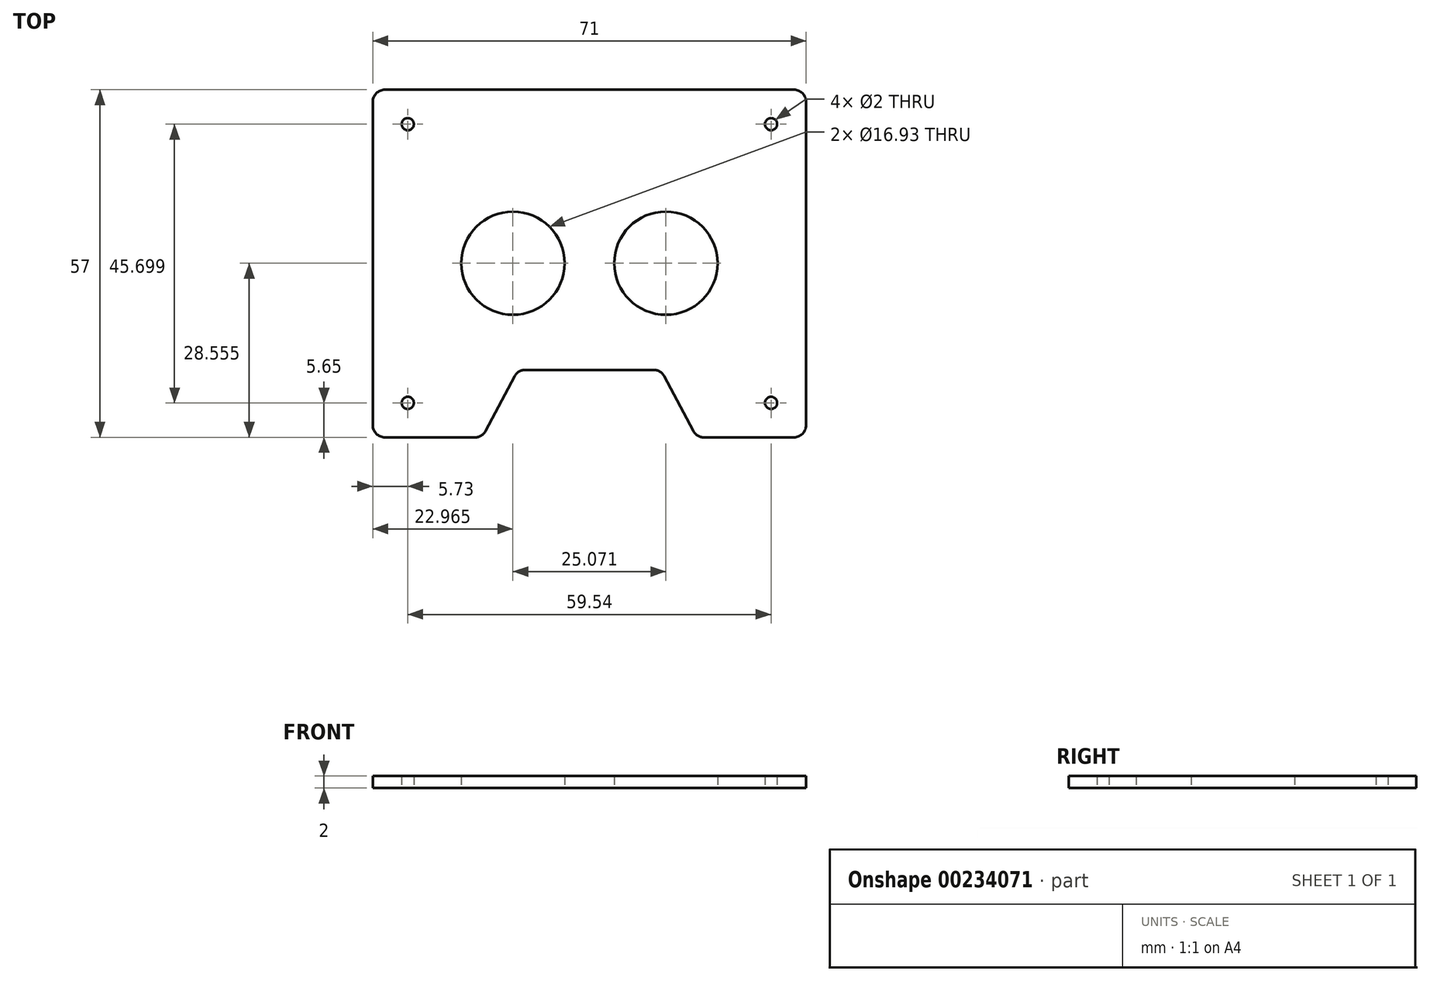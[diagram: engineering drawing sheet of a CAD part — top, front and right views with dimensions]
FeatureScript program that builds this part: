
annotation { "Feature Type Name" : "Feature", "Feature Type Description" : "" }
export const myFeature = defineFeature(function(context is Context, id is Id, definition is map)
    precondition{}
    {
        {
            var Q0;
            Q0=qCreatedBy(makeId("Top.planeOp"),FACE);
            var sketch = newSketch(context, id + "F0", { "sketchPlane" : qUnion([Q0])});
            skLineSegment(sketch, "E0.bottom", {"start": v(21, -8.5) * mm, "end": v(-21, -8.5) * mm, "construction": true});
            skLineSegment(sketch, "E0.top", {"start": v(21, 8.5) * mm, "end": v(-21, 8.5) * mm, "construction": true});
            skLineSegment(sketch, "E0.left", {"start": v(21, -8.5) * mm, "end": v(21, 8.5) * mm, "construction": true});
            skLineSegment(sketch, "E0.right", {"start": v(-21, -8.5) * mm, "end": v(-21, 8.5) * mm, "construction": true});
            skPoint(sketch, "E0.middle", {"position": v(0, 0) * mm});
            skLineSegment(sketch, "E1.bottom", {"start": v(35.5, -28.5) * mm, "end": v(17.56, -28.5) * mm});
            skLineSegment(sketch, "E1.top", {"start": v(35.5, 28.5) * mm, "end": v(-35.5, 28.5) * mm});
            skLineSegment(sketch, "E1.left", {"start": v(35.5, -28.5) * mm, "end": v(35.5, 28.5) * mm});
            skLineSegment(sketch, "E1.right", {"start": v(-35.5, -28.5) * mm, "end": v(-35.5, 28.5) * mm});
            skPoint(sketch, "E2", {"position": v(-29.77, 22.85) * mm});
            skPoint(sketch, "E3.MirrorP", {"position": v(29.77, 22.85) * mm});
            skPoint(sketch, "E4.MirrorP", {"position": v(-29.77, -22.85) * mm});
            skPoint(sketch, "E5.MirrorP", {"position": v(29.77, -22.85) * mm});
            skCircle(sketch, "E6", {"center": v(-12.54, 0.06) * mm, "radius": 8.46 * mm});
            skPoint(sketch, "E6.first.point", {"position": v(-21, 0) * mm});
            skPoint(sketch, "E6.second.point", {"position": v(-4.07, 0) * mm});
            skPoint(sketch, "E6.second.point.positionSnap0", {"position": v(-21, 0) * mm});
            skPoint(sketch, "E6.third.point", {"position": v(-11.96, 8.5) * mm});
            skPoint(sketch, "E7.MirrorP", {"position": v(4.07, 0) * mm});
            skCircle(sketch, "E8.MirrorC", {"center": v(12.54, 0.06) * mm, "radius": 8.46 * mm});
            skLineSegment(sketch, "E9", {"start": v(-17.56, -28.5) * mm, "end": v(-11.7, -17.43) * mm});
            skLineSegment(sketch, "E10", {"start": v(-11.7, -17.43) * mm, "end": v(0, -17.43) * mm});
            skLineSegment(sketch, "E11.MirrorCS", {"start": v(11.7, -17.43) * mm, "end": v(0, -17.43) * mm});
            skLineSegment(sketch, "E12.MirrorCS", {"start": v(17.56, -28.5) * mm, "end": v(11.7, -17.43) * mm});
            skLineSegment(sketch, "E13.trimOffspring", {"start": v(-17.56, -28.5) * mm, "end": v(-35.5, -28.5) * mm});
            skSolve(sketch);
        }
        {
            var Q0;
            Q0 = qSketchRegion(id + "F0", true);
            extrude(context, id + "F1", {"entities" : qUnion([Q0]), "depth" : 2 * mm});
        }
        {
            var Q0;
            Q0=makeQuery(id+"F1.opExtrude","SWEPT_EDGE",EDGE,{"disambiguationData":[OSD([sQuery(id+"F0.wireOp",EDGE,"E1.top"),sQuery(id+"F0.wireOp",EDGE,"E1.right")])]});
            var Q1;
            Q1=makeQuery(id+"F1.opExtrude","SWEPT_EDGE",EDGE,{"disambiguationData":[OSD([sQuery(id+"F0.wireOp",EDGE,"E1.right"),sQuery(id+"F0.wireOp",EDGE,"E13.trimOffspring")])]});
            var Q2;
            Q2=makeQuery(id+"F1.opExtrude","SWEPT_EDGE",EDGE,{"disambiguationData":[OSD([sQuery(id+"F0.wireOp",EDGE,"E9"),sQuery(id+"F0.wireOp",EDGE,"E13.trimOffspring")])]});
            var Q3;
            Q3=makeQuery(id+"F1.opExtrude","SWEPT_EDGE",EDGE,{"disambiguationData":[OSD([sQuery(id+"F0.wireOp",EDGE,"E9"),sQuery(id+"F0.wireOp",EDGE,"E10")])]});
            var Q4;
            Q4=makeQuery(id+"F1.opExtrude","SWEPT_EDGE",EDGE,{"disambiguationData":[OSD([sQuery(id+"F0.wireOp",EDGE,"E11.MirrorCS"),sQuery(id+"F0.wireOp",EDGE,"E12.MirrorCS")])]});
            var Q5;
            Q5=makeQuery(id+"F1.opExtrude","SWEPT_EDGE",EDGE,{"disambiguationData":[OSD([sQuery(id+"F0.wireOp",EDGE,"E1.bottom"),sQuery(id+"F0.wireOp",EDGE,"E12.MirrorCS")])]});
            var Q6;
            Q6=makeQuery(id+"F1.opExtrude","SWEPT_EDGE",EDGE,{"disambiguationData":[OSD([sQuery(id+"F0.wireOp",EDGE,"E1.bottom"),sQuery(id+"F0.wireOp",EDGE,"E1.left")])]});
            var Q7;
            Q7=makeQuery(id+"F1.opExtrude","SWEPT_EDGE",EDGE,{"disambiguationData":[OSD([sQuery(id+"F0.wireOp",EDGE,"E1.top"),sQuery(id+"F0.wireOp",EDGE,"E1.left")])]});
            fillet(context, id + "F2", {"entities" : qUnion([Q0, Q1, Q2, Q3, Q4, Q5, Q6, Q7]), "radius" : 2 * mm, "tangentPropagation" : true, "allowEdgeOverflow" : false});
        }
        {
            var Q0;
            Q0=sQuery(id+"F0.wireOp",VERTEX,"E2");
            var Q1;
            Q1=sQuery(id+"F0.wireOp",VERTEX,"E3.MirrorP");
            var Q2;
            Q2=sQuery(id+"F0.wireOp",VERTEX,"E5.MirrorP");
            var Q3;
            Q3=sQuery(id+"F0.wireOp",VERTEX,"E4.MirrorP");
            var Q4;
            Q4=makeQuery(id+"F1.opExtrude","SWEPT_BODY",BODY,{"disambiguationData":[OSD([sQuery(id+"F0.wireOp",EDGE,"E1.bottom"),sQuery(id+"F0.wireOp",EDGE,"E1.top"),sQuery(id+"F0.wireOp",EDGE,"E1.left"),sQuery(id+"F0.wireOp",EDGE,"E1.right"),sQuery(id+"F0.wireOp",EDGE,"E6"),sQuery(id+"F0.wireOp",EDGE,"E8.MirrorC"),sQuery(id+"F0.wireOp",EDGE,"E9"),sQuery(id+"F0.wireOp",EDGE,"E10"),sQuery(id+"F0.wireOp",EDGE,"E11.MirrorCS"),sQuery(id+"F0.wireOp",EDGE,"E12.MirrorCS"),sQuery(id+"F0.wireOp",EDGE,"E13.trimOffspring")])]});
            hole(context, id + "F3", {"style" : HoleStyle.SIMPLE, "endStyle" : HoleEndStyle.THROUGH, "oppositeDirection" : true, "holeDiameter" : 2 * mm, "locations" : qUnion([Q0, Q1, Q2, Q3]), "scope" : qUnion([Q4]), "isTappedThrough" : true});
        }
    });
